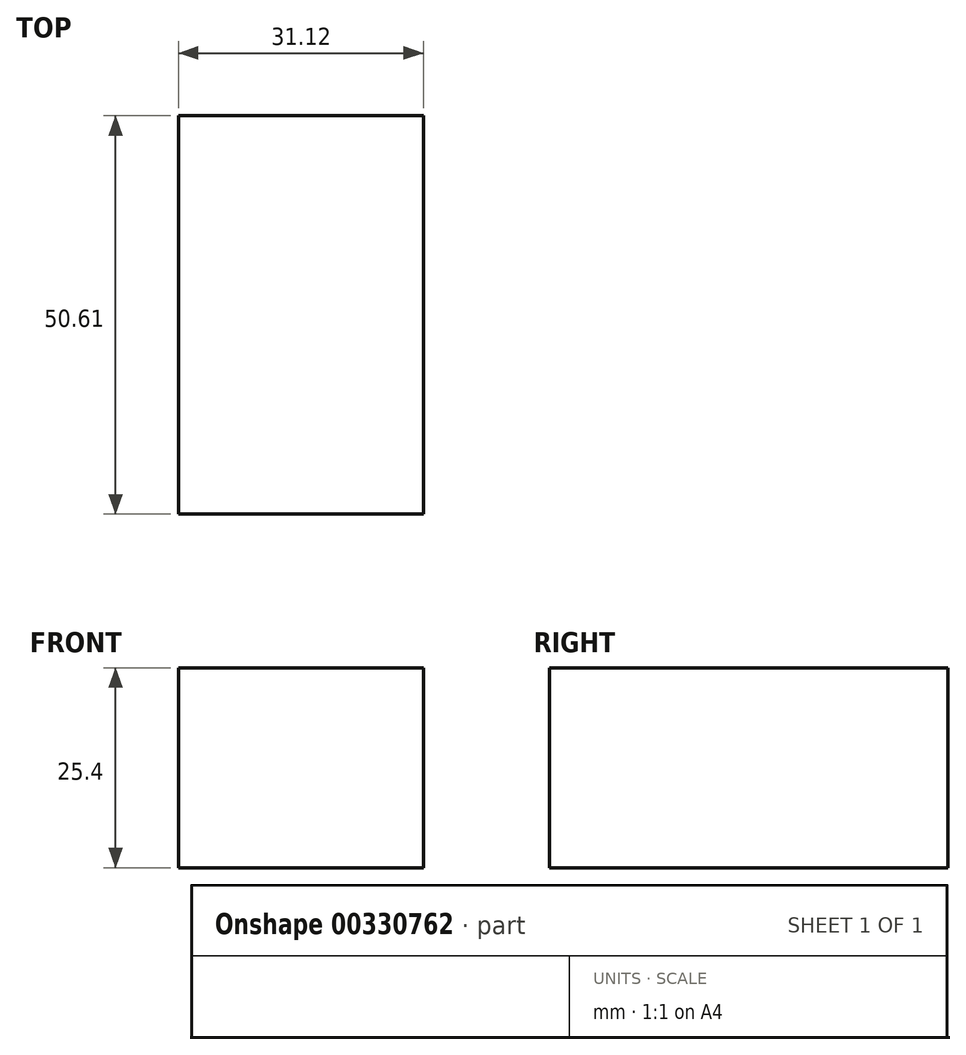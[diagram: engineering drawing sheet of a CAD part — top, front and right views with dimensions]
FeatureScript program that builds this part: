
annotation { "Feature Type Name" : "Feature", "Feature Type Description" : "" }
export const myFeature = defineFeature(function(context is Context, id is Id, definition is map)
    precondition{}
    {
        {
            var Q0;
            Q0=qCreatedBy(makeId("Top.planeOp"),FACE);
            var sketch = newSketch(context, id + "F0", { "sketchPlane" : qUnion([Q0])});
            skLineSegment(sketch, "E0.bottom", {"start": v(0, 0) * mm, "end": v(31.12, 0) * mm});
            skLineSegment(sketch, "E0.top", {"start": v(0, 50.61) * mm, "end": v(31.12, 50.61) * mm});
            skLineSegment(sketch, "E0.left", {"start": v(0, 0) * mm, "end": v(0, 50.61) * mm});
            skLineSegment(sketch, "E0.right", {"start": v(31.12, 0) * mm, "end": v(31.12, 50.61) * mm});
            skSolve(sketch);
        }
        {
            var Q0;
            Q0=makeQuery(id+"F0.imprint","IMPRINT",FACE,{"disambiguationData":[TD([[makeQuery(id+"F0.imprint","IMPRINT",EDGE,{"derivedFrom":sQuery(id+"F0.wireOp",EDGE,"E0.bottom")}),1.0]])]});
            var sketch = newSketch(context, id + "F1", { "sketchPlane" : qUnion([Q0])});
            skSolve(sketch);
        }
        {
            var Q0;
            Q0=makeQuery(id+"F1.imprint","IMPRINT",FACE,{"disambiguationData":[TD([[makeQuery(id+"F1.imprint","IMPRINT",EDGE,{"derivedFrom":makeQuery(id+"F0.imprint","IMPRINT",EDGE,{"derivedFrom":sQuery(id+"F0.wireOp",EDGE,"E0.bottom")})}),1.0]])]});
            extrude(context, id + "F2", {"entities" : qUnion([Q0]), "depth" : 25.4 * mm, "offsetDistance" : 25.4 * mm});
        }
    });
